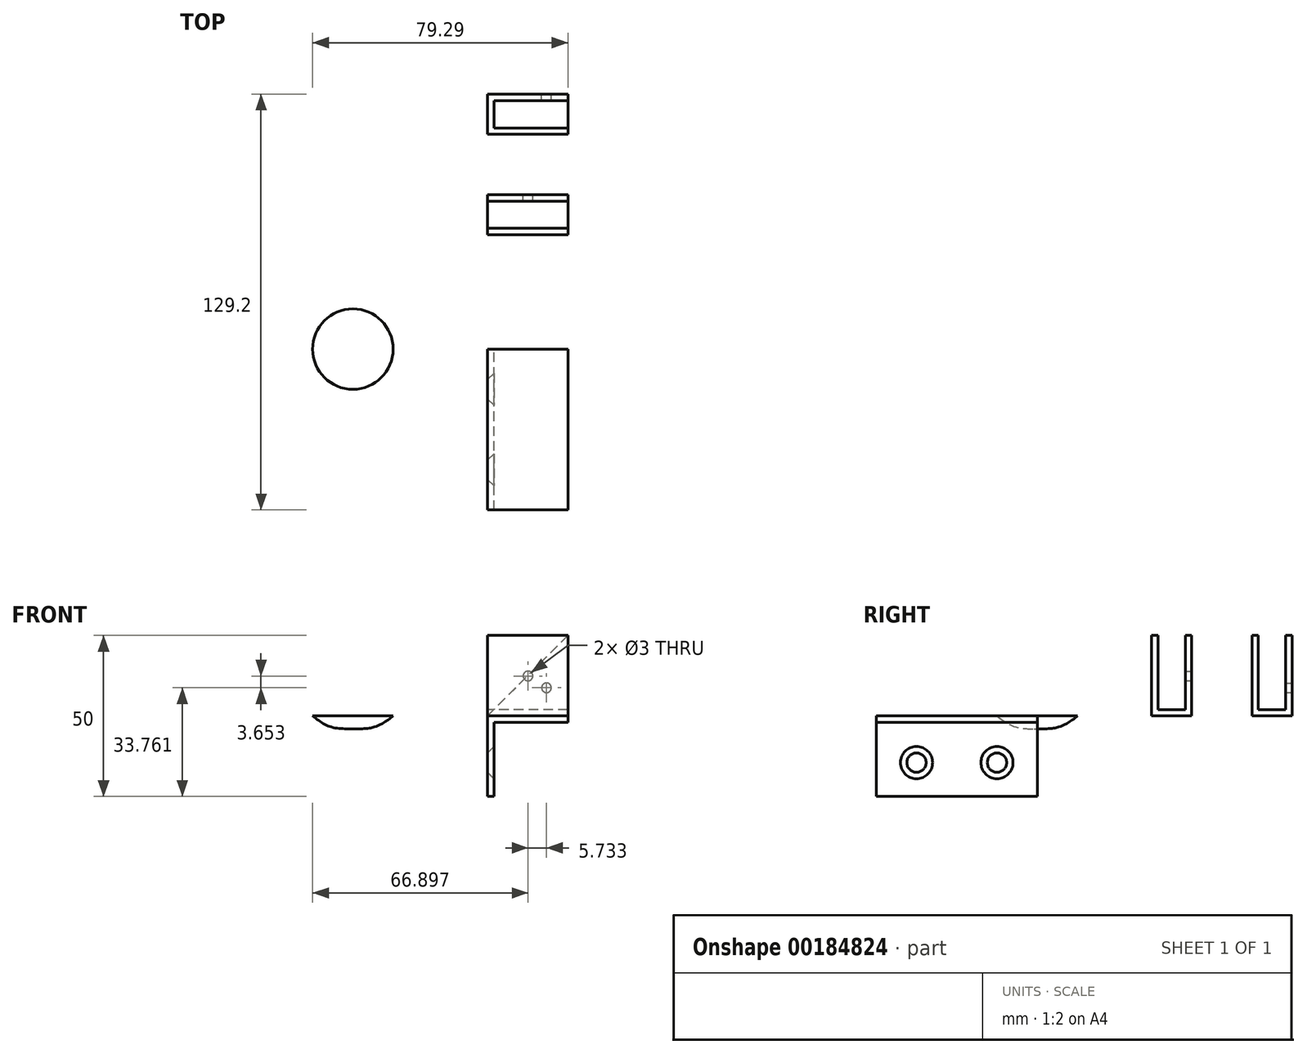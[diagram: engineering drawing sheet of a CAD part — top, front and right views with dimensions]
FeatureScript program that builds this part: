
annotation { "Feature Type Name" : "Feature", "Feature Type Description" : "" }
export const myFeature = defineFeature(function(context is Context, id is Id, definition is map)
    precondition{}
    {
        {
            var Q0;
            Q0=qCreatedBy(makeId("Front.planeOp"),FACE);
            var sketch = newSketch(context, id + "F0", { "sketchPlane" : qUnion([Q0])});
            skLineSegment(sketch, "E0", {"start": v(25, 0) * mm, "end": v(0, 0) * mm});
            skLineSegment(sketch, "E1", {"start": v(0, 0) * mm, "end": v(0, -25) * mm});
            skLineSegment(sketch, "E2.0", {"start": v(2, -2) * mm, "end": v(2, -25) * mm});
            skLineSegment(sketch, "E2.1", {"start": v(25, -2) * mm, "end": v(2, -2) * mm});
            skLineSegment(sketch, "E3", {"start": v(25, -2) * mm, "end": v(25, 0) * mm});
            skLineSegment(sketch, "E4", {"start": v(2, -25) * mm, "end": v(0, -25) * mm});
            skSolve(sketch);
        }
        {
            var Q0;
            Q0=makeQuery(id+"F0.imprint","IMPRINT",FACE,{"disambiguationData":[TD([[makeQuery(id+"F0.imprint","IMPRINT",EDGE,{"derivedFrom":sQuery(id+"F0.wireOp",EDGE,"E0")}),1.0]])]});
            extrude(context, id + "F1", {"entities" : qUnion([Q0]), "depth" : 50 * mm});
        }
        {
            var Q0;
            Q0=makeQuery(id+"F1.opExtrude","SWEPT_FACE",FACE,{"disambiguationData":[OSD([sQuery(id+"F0.wireOp",EDGE,"E2.0")])]});
            var sketch = newSketch(context, id + "F2", { "sketchPlane" : qUnion([Q0])});
            skCircle(sketch, "E5.2.0.0", {"center": v(62.5, 12.5) * mm, "radius": 1.5 * mm});
            skCircle(sketch, "E6", {"center": v(-37.5, -14.5) * mm, "radius": 2.75 * mm});
            skCircle(sketch, "E7.1.0.0", {"center": v(-12.5, -14.5) * mm, "radius": 2.75 * mm});
            skLineSegment(sketch, "E7.direction1", {"start": v(-37.5, -14.5) * mm, "end": v(-12.5, -14.5) * mm, "construction": true});
            skSolve(sketch);
        }
        {
            var Q0;
            Q0=sQuery(id+"F2.wireOp",VERTEX,"E6.center");
            var Q1;
            Q1=sQuery(id+"F2.wireOp",VERTEX,"E7.1.0.0.center");
            var Q2;
            Q2=makeQuery(id+"F1.opExtrude","SWEPT_BODY",BODY,{"disambiguationData":[OSD([sQuery(id+"F0.wireOp",EDGE,"E0"),sQuery(id+"F0.wireOp",EDGE,"E1"),sQuery(id+"F0.wireOp",EDGE,"E2.0"),sQuery(id+"F0.wireOp",EDGE,"E2.1"),sQuery(id+"F0.wireOp",EDGE,"E3"),sQuery(id+"F0.wireOp",EDGE,"E4")])]});
            hole(context, id + "F3", {"style" : HoleStyle.C_SINK, "endStyle" : HoleEndStyle.THROUGH, "holeDiameter" : 5 * mm, "cSinkDiameter" : 10 * mm, "cSinkAngle" : 90 * degree, "locations" : qUnion([Q0, Q1]), "scope" : qUnion([Q2]), "isTappedThrough" : true});
        }
        {
            var Q0;
            Q0=qCreatedBy(makeId("Front.planeOp"),FACE);
            var sketch = newSketch(context, id + "F4", { "sketchPlane" : qUnion([Q0])});
            skLineSegment(sketch, "E8", {"start": v(-54.29, 0) * mm, "end": v(-41.79, 0) * mm});
            skLineSegment(sketch, "E9", {"start": v(-41.79, 0) * mm, "end": v(-41.79, -4) * mm});
            skFitSpline(sketch, "E10", {"points": [v(-41.79, -4) * mm, v(-48.88, -3.31) * mm, v(-54.29, 0) * mm], "startDerivative": vector(-14.45, -0.07) * mm, "endDerivative": vector(-10.5, 8.15) * mm});
            skSolve(sketch);
        }
        {
            var Q0;
            Q0=makeQuery(id+"F4.imprint","IMPRINT",FACE,{"disambiguationData":[TD([[makeQuery(id+"F4.imprint","IMPRINT",EDGE,{"derivedFrom":sQuery(id+"F4.wireOp",EDGE,"E8")}),-1.0]])]});
            var Q1;
            Q1=sQuery(id+"F4.wireOp",EDGE,"E9");
            revolve(context, id + "F5", {"entities" : qUnion([Q0]), "axis" : qUnion([Q1]), "revolveType" : RevolveType.FULL});
        }
        {
            var Q0;
            Q0=qCreatedBy(makeId("Right.planeOp"),FACE);
            var sketch = newSketch(context, id + "F6", { "sketchPlane" : qUnion([Q0])});
            skLineSegment(sketch, "E11", {"start": v(66.7, 25) * mm, "end": v(66.7, 0) * mm});
            skLineSegment(sketch, "E12", {"start": v(66.7, 0) * mm, "end": v(79.2, 0) * mm});
            skLineSegment(sketch, "E13", {"start": v(79.2, 0) * mm, "end": v(79.2, 25) * mm});
            skLineSegment(sketch, "E14.0", {"start": v(77.2, 2) * mm, "end": v(77.2, 25) * mm});
            skLineSegment(sketch, "E14.1", {"start": v(68.7, 2) * mm, "end": v(77.2, 2) * mm});
            skLineSegment(sketch, "E14.2", {"start": v(68.7, 25) * mm, "end": v(68.7, 2) * mm});
            skLineSegment(sketch, "E15", {"start": v(66.7, 25) * mm, "end": v(68.7, 25) * mm});
            skLineSegment(sketch, "E16", {"start": v(77.2, 25) * mm, "end": v(79.2, 25) * mm});
            skSolve(sketch);
        }
        {
            var Q0;
            Q0 = qSketchRegion(id + "F6", true);
            extrude(context, id + "F7", {"entities" : qUnion([Q0]), "depth" : 25 * mm});
        }
        {
            var Q0;
            Q0=makeQuery(id+"F7.opExtrude","SWEPT_FACE",FACE,{"disambiguationData":[OSD([sQuery(id+"F6.wireOp",EDGE,"E13")])]});
            var sketch = newSketch(context, id + "F8", { "sketchPlane" : qUnion([Q0])});
            skLineSegment(sketch, "E17", {"start": v(-25, 25) * mm, "end": v(0, 0) * mm});
            skLineSegment(sketch, "E18", {"start": v(0, 0) * mm, "end": v(0, 25) * mm});
            skLineSegment(sketch, "E19", {"start": v(0, 25) * mm, "end": v(-23, 25) * mm});
            skLineSegment(sketch, "E20", {"start": v(-23, 25) * mm, "end": v(-25, 25) * mm});
            skSolve(sketch);
        }
        {
            var Q0;
            Q0=makeQuery(id+"F8.imprint","IMPRINT",FACE,{"disambiguationData":[TD([[makeQuery(id+"F8.imprint","IMPRINT",EDGE,{"derivedFrom":sQuery(id+"F8.wireOp",EDGE,"E17")}),1.0]])]});
            extrude(context, id + "F9", {"entities" : qUnion([Q0]), "operationType" : NewBodyOperationType.REMOVE, "oppositeDirection" : true, "depth" : 25 * mm});
        }
        {
            var Q0;
            Q0=qCreatedBy(makeId("Right.planeOp"),FACE);
            var sketch = newSketch(context, id + "F10", { "sketchPlane" : qUnion([Q0])});
            skLineSegment(sketch, "E21", {"start": v(35.5, 25) * mm, "end": v(35.5, 0) * mm});
            skLineSegment(sketch, "E22", {"start": v(35.5, 0) * mm, "end": v(48, 0) * mm});
            skLineSegment(sketch, "E23", {"start": v(48, 0) * mm, "end": v(48, 25) * mm});
            skLineSegment(sketch, "E24.0", {"start": v(46, 2) * mm, "end": v(46, 25) * mm});
            skLineSegment(sketch, "E24.1", {"start": v(37.5, 2) * mm, "end": v(46, 2) * mm});
            skLineSegment(sketch, "E24.2", {"start": v(37.5, 25) * mm, "end": v(37.5, 2) * mm});
            skLineSegment(sketch, "E25", {"start": v(35.5, 25) * mm, "end": v(37.5, 25) * mm});
            skLineSegment(sketch, "E26", {"start": v(46, 25) * mm, "end": v(48, 25) * mm});
            skSolve(sketch);
        }
        {
            var Q0;
            Q0=makeQuery(id+"F10.imprint","IMPRINT",FACE,{"disambiguationData":[TD([[makeQuery(id+"F10.imprint","IMPRINT",EDGE,{"derivedFrom":sQuery(id+"F10.wireOp",EDGE,"E21")}),1.0]])]});
            extrude(context, id + "F11", {"entities" : qUnion([Q0]), "depth" : 25 * mm});
        }
        {
            var Q0;
            Q0=makeQuery(id+"F7.opExtrude","SWEPT_FACE",FACE,{"disambiguationData":[OSD([sQuery(id+"F6.wireOp",EDGE,"E13")])]});
            var sketch = newSketch(context, id + "F12", { "sketchPlane" : qUnion([Q0])});
            skCircle(sketch, "E27", {"center": v(-18.34, 8.76) * mm, "radius": 2.28 * mm});
            skSolve(sketch);
        }
        {
            var Q0;
            Q0=makeQuery(id+"F11.opExtrude","SWEPT_FACE",FACE,{"disambiguationData":[OSD([sQuery(id+"F10.wireOp",EDGE,"E23")])]});
            var sketch = newSketch(context, id + "F13", { "sketchPlane" : qUnion([Q0])});
            skCircle(sketch, "E28", {"center": v(-12.6, 12.41) * mm, "radius": 3.14 * mm});
            skSolve(sketch);
        }
        {
            var Q0;
            Q0=sQuery(id+"F12.wireOp",VERTEX,"E27.center");
            var Q1;
            Q1=makeQuery(id+"F7.opExtrude","SWEPT_BODY",BODY,{"disambiguationData":[OSD([sQuery(id+"F6.wireOp",EDGE,"E11"),sQuery(id+"F6.wireOp",EDGE,"E12"),sQuery(id+"F6.wireOp",EDGE,"E13"),sQuery(id+"F6.wireOp",EDGE,"E14.0"),sQuery(id+"F6.wireOp",EDGE,"E14.1"),sQuery(id+"F6.wireOp",EDGE,"E14.2"),sQuery(id+"F6.wireOp",EDGE,"E15"),sQuery(id+"F6.wireOp",EDGE,"E16")])]});
            hole(context, id + "F14", {"style" : HoleStyle.SIMPLE, "endStyle" : HoleEndStyle.BLIND, "holeDiameter" : 3 * mm, "holeDepth" : 5 * mm, "locations" : qUnion([Q0]), "scope" : qUnion([Q1])});
        }
        {
            var Q0;
            Q0=sQuery(id+"F13.wireOp",VERTEX,"E28.center");
            var Q1;
            Q1=makeQuery(id+"F11.opExtrude","SWEPT_BODY",BODY,{"disambiguationData":[OSD([sQuery(id+"F10.wireOp",EDGE,"E21"),sQuery(id+"F10.wireOp",EDGE,"E22"),sQuery(id+"F10.wireOp",EDGE,"E23"),sQuery(id+"F10.wireOp",EDGE,"E24.0"),sQuery(id+"F10.wireOp",EDGE,"E24.1"),sQuery(id+"F10.wireOp",EDGE,"E24.2"),sQuery(id+"F10.wireOp",EDGE,"E25"),sQuery(id+"F10.wireOp",EDGE,"E26")])]});
            hole(context, id + "F15", {"style" : HoleStyle.SIMPLE, "endStyle" : HoleEndStyle.BLIND, "holeDiameter" : 3 * mm, "holeDepth" : 5 * mm, "locations" : qUnion([Q0]), "scope" : qUnion([Q1])});
        }
    });
